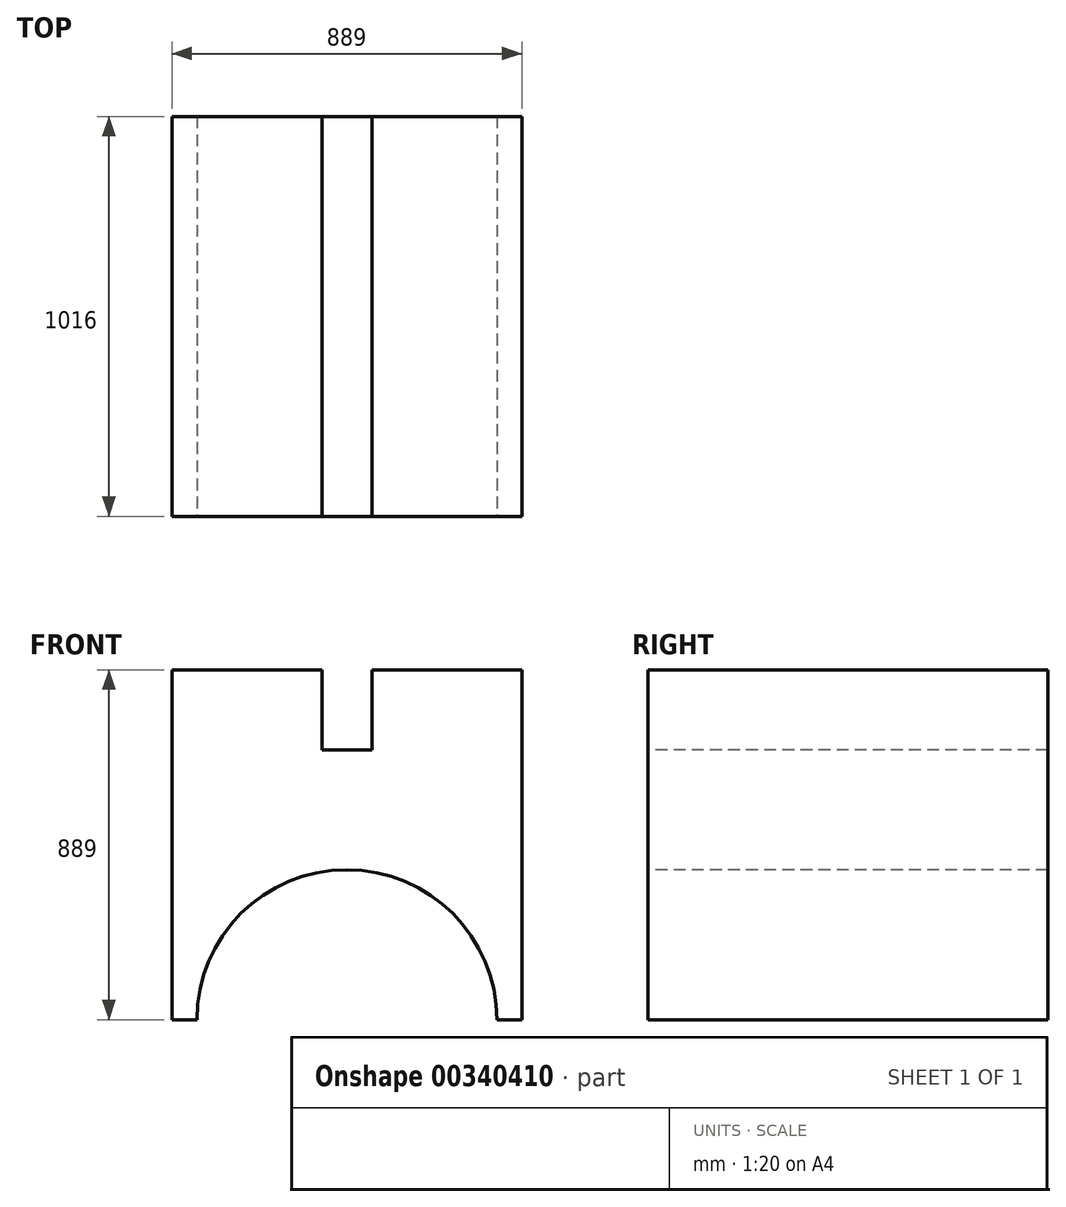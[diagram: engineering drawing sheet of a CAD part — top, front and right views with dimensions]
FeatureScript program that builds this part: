
annotation { "Feature Type Name" : "Feature", "Feature Type Description" : "" }
export const myFeature = defineFeature(function(context is Context, id is Id, definition is map)
    precondition{}
    {
        {
            var Q0;
            Q0=qCreatedBy(makeId("Right.planeOp"),FACE);
            var sketch = newSketch(context, id + "F0", { "sketchPlane" : qUnion([Q0])});
            skLineSegment(sketch, "E0", {"start": v(0, 0) * mm, "end": v(1016, 0) * mm});
            skLineSegment(sketch, "E1", {"start": v(1016, 0) * mm, "end": v(1016, 889) * mm});
            skLineSegment(sketch, "E2", {"start": v(1016, 889) * mm, "end": v(0, 889) * mm});
            skLineSegment(sketch, "E3", {"start": v(0, 889) * mm, "end": v(0, 0) * mm});
            skSolve(sketch);
        }
        {
            var Q0;
            Q0 = qSketchRegion(id + "F0", true);
            extrude(context, id + "F1", {"entities" : qUnion([Q0]), "depth" : 889 * mm});
        }
        {
            var Q0;
            Q0=makeQuery(id+"F1.opExtrude","SWEPT_FACE",FACE,{"disambiguationData":[OSD([sQuery(id+"F0.wireOp",EDGE,"E3")])]});
            var sketch = newSketch(context, id + "F2", { "sketchPlane" : qUnion([Q0])});
            skLineSegment(sketch, "E4", {"start": v(0, 0) * mm, "end": v(63.5, 0) * mm});
            skLineSegment(sketch, "E5", {"start": v(0, 0) * mm, "end": v(0, 889) * mm});
            skLineSegment(sketch, "E6", {"start": v(0, 889) * mm, "end": v(381, 889) * mm});
            skLineSegment(sketch, "E7", {"start": v(381, 889) * mm, "end": v(381, 685.8) * mm});
            skLineSegment(sketch, "E8", {"start": v(381, 685.8) * mm, "end": v(508, 685.8) * mm});
            skLineSegment(sketch, "E9", {"start": v(508, 685.8) * mm, "end": v(508, 889) * mm});
            skLineSegment(sketch, "E10", {"start": v(508, 889) * mm, "end": v(889, 889) * mm});
            skLineSegment(sketch, "E11", {"start": v(889, 889) * mm, "end": v(889, 0) * mm});
            skLineSegment(sketch, "E12", {"start": v(889, 0) * mm, "end": v(825.5, 0) * mm});
            skArc(sketch, "E13", {"start": v(825.5, 0) * mm, "mid": v(444.5, 381) * mm, "end": v(63.5, 0) * mm});
            skSolve(sketch);
        }
        {
            var Q0;
            {var subQ0=sQuery(id+"F2.wireOp",EDGE,"E13");Q0=makeQuery(id+"F2.imprint","IMPRINT",FACE,{"disambiguationData":[TD([[makeQuery(id+"F2.imprint","IMPRINT",EDGE,{"derivedFrom":subQ0}),1.0]])]});}
            var Q1;
            {var subQ0=sQuery(id+"F2.wireOp",EDGE,"E7");Q1=makeQuery(id+"F2.imprint","IMPRINT",FACE,{"disambiguationData":[TD([[makeQuery(id+"F2.imprint","IMPRINT",EDGE,{"derivedFrom":subQ0}),1.0]])]});}
            extrude(context, id + "F3", {"entities" : qUnion([Q0, Q1]), "operationType" : NewBodyOperationType.REMOVE, "endBound" : BoundingType.THROUGH_ALL, "oppositeDirection" : true, "depth" : 25.4 * mm});
        }
    });
